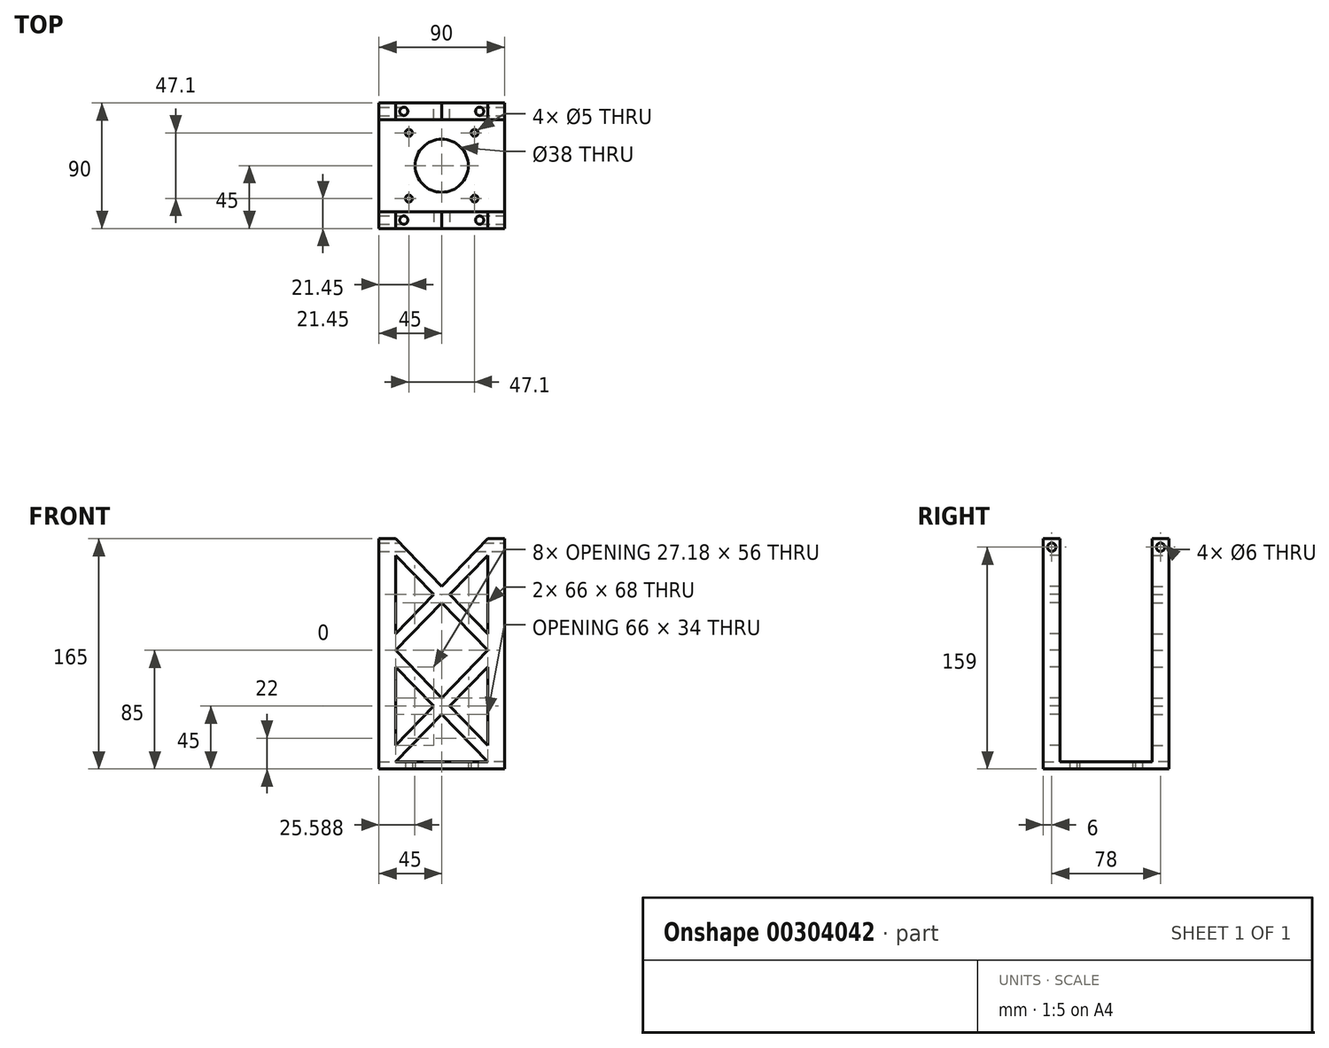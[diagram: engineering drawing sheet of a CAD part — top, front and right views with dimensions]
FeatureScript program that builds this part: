
annotation { "Feature Type Name" : "Feature", "Feature Type Description" : "" }
export const myFeature = defineFeature(function(context is Context, id is Id, definition is map)
    precondition{}
    {
        {
            var Q0;
            Q0=qCreatedBy(makeId("Top.planeOp"),FACE);
            var sketch = newSketch(context, id + "F0", { "sketchPlane" : qUnion([Q0])});
            skLineSegment(sketch, "E0.bottom", {"start": v(45, -45) * mm, "end": v(-45, -45) * mm});
            skLineSegment(sketch, "E0.top", {"start": v(45, 45) * mm, "end": v(-45, 45) * mm});
            skLineSegment(sketch, "E0.left", {"start": v(45, -45) * mm, "end": v(45, 45) * mm});
            skLineSegment(sketch, "E0.right", {"start": v(-45, -45) * mm, "end": v(-45, 45) * mm});
            skPoint(sketch, "E0.middle", {"position": v(0, 0) * mm});
            skLineSegment(sketch, "E1.bottom", {"start": v(23.55, -23.55) * mm, "end": v(-23.55, -23.55) * mm, "construction": true});
            skLineSegment(sketch, "E1.top", {"start": v(23.55, 23.55) * mm, "end": v(-23.55, 23.55) * mm, "construction": true});
            skLineSegment(sketch, "E1.left", {"start": v(23.55, -23.55) * mm, "end": v(23.55, 23.55) * mm, "construction": true});
            skLineSegment(sketch, "E1.right", {"start": v(-23.55, -23.55) * mm, "end": v(-23.55, 23.55) * mm, "construction": true});
            skCircle(sketch, "E2", {"center": v(0, 0) * mm, "radius": 19 * mm});
            skCircle(sketch, "E3", {"center": v(-23.55, 23.55) * mm, "radius": 2.5 * mm});
            skCircle(sketch, "E4", {"center": v(23.55, 23.55) * mm, "radius": 2.5 * mm});
            skCircle(sketch, "E5", {"center": v(23.55, -23.55) * mm, "radius": 2.5 * mm});
            skCircle(sketch, "E6", {"center": v(-23.55, -23.55) * mm, "radius": 2.5 * mm});
            skSolve(sketch);
        }
        {
            var Q0;
            Q0=makeQuery(id+"F0.imprint","IMPRINT",FACE,{"disambiguationData":[TD([[makeQuery(id+"F0.imprint","IMPRINT",EDGE,{"derivedFrom":sQuery(id+"F0.wireOp",EDGE,"E0.bottom")}),-1.0]])]});
            extrude(context, id + "F1", {"entities" : qUnion([Q0]), "depth" : 5 * mm});
        }
        {
            var Q0;
            Q0=makeQuery(id+"F1.opExtrude","CAP_FACE",FACE,{"disambiguationData":[OSD([sQuery(id+"F0.wireOp",EDGE,"E0.bottom"),sQuery(id+"F0.wireOp",EDGE,"E0.top"),sQuery(id+"F0.wireOp",EDGE,"E0.left"),sQuery(id+"F0.wireOp",EDGE,"E0.right"),sQuery(id+"F0.wireOp",EDGE,"E2"),sQuery(id+"F0.wireOp",EDGE,"E3"),sQuery(id+"F0.wireOp",EDGE,"E4"),sQuery(id+"F0.wireOp",EDGE,"E5"),sQuery(id+"F0.wireOp",EDGE,"E6")])],"isStart":false});
            cPlane(context, id + "F2", {"entities" : qUnion([Q0]), "cplaneType" : CPlaneType.OFFSET, "offset" : 0 * mm, "width" : 150 * mm, "height" : 150 * mm});
        }
        {
            var Q0;
            Q0=qCreatedBy(id+"F2.planeOp",FACE);
            var sketch = newSketch(context, id + "F3", { "sketchPlane" : qUnion([Q0])});
            skPoint(sketch, "E7.0", {"position": v(-45, -45) * mm});
            skLineSegment(sketch, "E8.bottom", {"start": v(-45, -45) * mm, "end": v(-33, -45) * mm});
            skLineSegment(sketch, "E8.top", {"start": v(-45, -33) * mm, "end": v(-33, -33) * mm});
            skLineSegment(sketch, "E8.left", {"start": v(-45, -45) * mm, "end": v(-45, -33) * mm});
            skLineSegment(sketch, "E8.right", {"start": v(-33, -45) * mm, "end": v(-33, -33) * mm});
            skPoint(sketch, "E9.1.0", {"position": v(45, -45) * mm});
            skLineSegment(sketch, "E9.1.1", {"start": v(45, -33) * mm, "end": v(33, -33) * mm});
            skLineSegment(sketch, "E9.1.2", {"start": v(45, -45) * mm, "end": v(33, -45) * mm});
            skLineSegment(sketch, "E9.1.3", {"start": v(33, -45) * mm, "end": v(33, -33) * mm});
            skLineSegment(sketch, "E9.1.4", {"start": v(45, -45) * mm, "end": v(45, -33) * mm});
            skPoint(sketch, "E9.2.0", {"position": v(45, 45) * mm});
            skLineSegment(sketch, "E9.2.1", {"start": v(33, 45) * mm, "end": v(33, 33) * mm});
            skLineSegment(sketch, "E9.2.2", {"start": v(45, 45) * mm, "end": v(45, 33) * mm});
            skLineSegment(sketch, "E9.2.3", {"start": v(45, 33) * mm, "end": v(33, 33) * mm});
            skLineSegment(sketch, "E9.2.4", {"start": v(45, 45) * mm, "end": v(33, 45) * mm});
            skPoint(sketch, "E9.3.0", {"position": v(-45, 45) * mm});
            skLineSegment(sketch, "E9.3.1", {"start": v(-45, 33) * mm, "end": v(-33, 33) * mm});
            skLineSegment(sketch, "E9.3.2", {"start": v(-45, 45) * mm, "end": v(-33, 45) * mm});
            skLineSegment(sketch, "E9.3.3", {"start": v(-33, 45) * mm, "end": v(-33, 33) * mm});
            skLineSegment(sketch, "E9.3.4", {"start": v(-45, 45) * mm, "end": v(-45, 33) * mm});
            skPoint(sketch, "E9.center", {"position": v(0, 0) * mm});
            skSolve(sketch);
        }
        {
            var Q0;
            Q0=makeQuery(id+"F3.imprint","IMPRINT",FACE,{"disambiguationData":[TD([[makeQuery(id+"F3.imprint","IMPRINT",EDGE,{"derivedFrom":sQuery(id+"F3.wireOp",EDGE,"E8.bottom")}),1.0]])]});
            var Q1;
            Q1=makeQuery(id+"F3.imprint","IMPRINT",FACE,{"disambiguationData":[TD([[makeQuery(id+"F3.imprint","IMPRINT",EDGE,{"derivedFrom":sQuery(id+"F3.wireOp",EDGE,"E9.1.1")}),1.0]])]});
            var Q2;
            Q2=makeQuery(id+"F3.imprint","IMPRINT",FACE,{"disambiguationData":[TD([[makeQuery(id+"F3.imprint","IMPRINT",EDGE,{"derivedFrom":sQuery(id+"F3.wireOp",EDGE,"E9.2.1")}),1.0]])]});
            var Q3;
            Q3=makeQuery(id+"F3.imprint","IMPRINT",FACE,{"disambiguationData":[TD([[makeQuery(id+"F3.imprint","IMPRINT",EDGE,{"derivedFrom":sQuery(id+"F3.wireOp",EDGE,"E9.3.1")}),1.0]])]});
            extrude(context, id + "F4", {"entities" : qUnion([Q0, Q1, Q2, Q3]), "operationType" : NewBodyOperationType.ADD, "depth" : 160 * mm});
        }
        {
            var Q0;
            Q0=makeQuery(id+"F4.boolean.opBoolean","MERGE",FACE,{"derivedFrom":[makeQuery(id+"F1.opExtrude","SWEPT_FACE",FACE,{"disambiguationData":[OSD([sQuery(id+"F0.wireOp",EDGE,"E0.bottom")])]}),makeQuery(id+"F4.opExtrude","SWEPT_FACE",FACE,{"disambiguationData":[OSD([sQuery(id+"F3.wireOp",EDGE,"E8.bottom")])]}),makeQuery(id+"F4.opExtrude","SWEPT_FACE",FACE,{"disambiguationData":[OSD([sQuery(id+"F3.wireOp",EDGE,"E9.1.2")])]})]});
            cPlane(context, id + "F5", {"entities" : qUnion([Q0]), "cplaneType" : CPlaneType.OFFSET, "offset" : 0 * mm, "width" : 150 * mm, "height" : 150 * mm});
        }
        {
            var Q0;
            Q0=qCreatedBy(id+"F5.planeOp",FACE);
            var sketch = newSketch(context, id + "F6", { "sketchPlane" : qUnion([Q0])});
            skPoint(sketch, "E10.0", {"position": v(-33, 5) * mm});
            skLineSegment(sketch, "E11", {"start": v(-33, 5) * mm, "end": v(-33, 17) * mm});
            skLineSegment(sketch, "E12", {"start": v(-33, 45) * mm, "end": v(33, 45) * mm, "construction": true});
            skLineSegment(sketch, "E13", {"start": v(0, 0) * mm, "end": v(0, 167.46) * mm, "construction": true});
            skLineSegment(sketch, "E14.0", {"start": v(-33, 85) * mm, "end": v(33, 85) * mm, "construction": true});
            skLineSegment(sketch, "E15.MirrorCS", {"start": v(33, 5) * mm, "end": v(33, 17) * mm});
            skLineSegment(sketch, "E16.MirrorCS", {"start": v(-33, 85) * mm, "end": v(-33, 73) * mm});
            skLineSegment(sketch, "E17.MirrorCS", {"start": v(33, 85) * mm, "end": v(33, 73) * mm});
            skLineSegment(sketch, "E18", {"start": v(-33, 5) * mm, "end": v(33, 73) * mm});
            skLineSegment(sketch, "E19", {"start": v(-33, 17) * mm, "end": v(33, 85) * mm});
            skLineSegment(sketch, "E20", {"start": v(33, 5) * mm, "end": v(-33, 73) * mm});
            skLineSegment(sketch, "E21", {"start": v(33, 17) * mm, "end": v(-33, 85) * mm});
            skLineSegment(sketch, "E22.MirrorCS", {"start": v(33, 153) * mm, "end": v(-33, 85) * mm});
            skLineSegment(sketch, "E23.MirrorCS", {"start": v(33, 165) * mm, "end": v(-33, 97) * mm});
            skLineSegment(sketch, "E24.MirrorCS", {"start": v(-33, 153) * mm, "end": v(33, 85) * mm});
            skLineSegment(sketch, "E25.MirrorCS", {"start": v(-33, 165) * mm, "end": v(33, 97) * mm});
            skLineSegment(sketch, "E26.MirrorCS", {"start": v(-33, 85) * mm, "end": v(-33, 97) * mm});
            skLineSegment(sketch, "E27.MirrorCS", {"start": v(-33, 165) * mm, "end": v(-33, 153) * mm});
            skLineSegment(sketch, "E28.MirrorCS", {"start": v(33, 165) * mm, "end": v(33, 153) * mm});
            skLineSegment(sketch, "E29.MirrorCS", {"start": v(33, 85) * mm, "end": v(33, 97) * mm});
            skSolve(sketch);
        }
        {
            var Q0;
            {var subQ0=sQuery(id+"F6.wireOp",EDGE,"E17.MirrorCS");Q0=makeQuery(id+"F6.imprint","IMPRINT",FACE,{"disambiguationData":[TD([[makeQuery(id+"F6.imprint","IMPRINT",EDGE,{"derivedFrom":subQ0}),-1.0]])]});}
            var Q1;
            {var subQ5=sQuery(id+"F6.wireOp",EDGE,"E29.MirrorCS");Q1=makeQuery(id+"F6.imprint","IMPRINT",FACE,{"disambiguationData":[TD([[makeQuery(id+"F6.imprint","IMPRINT",EDGE,{"derivedFrom":subQ5}),1.0]])]});}
            var Q2;
            {var subQ0=sQuery(id+"F6.wireOp",EDGE,"E28.MirrorCS");Q2=makeQuery(id+"F6.imprint","IMPRINT",FACE,{"disambiguationData":[TD([[makeQuery(id+"F6.imprint","IMPRINT",EDGE,{"derivedFrom":subQ0}),-1.0]])]});}
            var Q3;
            {var subQ5=sQuery(id+"F6.wireOp",EDGE,"E27.MirrorCS");Q3=makeQuery(id+"F6.imprint","IMPRINT",FACE,{"disambiguationData":[TD([[makeQuery(id+"F6.imprint","IMPRINT",EDGE,{"derivedFrom":subQ5}),1.0]])]});}
            var Q4;
            {var subQ0=sQuery(id+"F6.wireOp",EDGE,"E26.MirrorCS");Q4=makeQuery(id+"F6.imprint","IMPRINT",FACE,{"disambiguationData":[TD([[makeQuery(id+"F6.imprint","IMPRINT",EDGE,{"derivedFrom":subQ0}),-1.0]])]});}
            var Q5;
            {var subQ0=sQuery(id+"F6.wireOp",EDGE,"E25.MirrorCS");var subQ1=sQuery(id+"F6.wireOp",EDGE,"E22.MirrorCS");var subQ2=makeQuery(id+"F6.imprint","INTERSECT",VERTEX,{"derivedFrom":[subQ1,subQ0]});Q5=makeQuery(id+"F6.imprint","IMPRINT",FACE,{"disambiguationData":[TD([[makeQuery(id+"F6.imprint","IMPRINT",EDGE,{"disambiguationData":[TD([[subQ2,-1.0]])],"derivedFrom":subQ1}),-1.0]])]});}
            var Q6;
            {var subQ0=sQuery(id+"F6.wireOp",EDGE,"E20");var subQ1=sQuery(id+"F6.wireOp",EDGE,"E18");var subQ2=makeQuery(id+"F6.imprint","INTERSECT",VERTEX,{"derivedFrom":[subQ1,subQ0]});Q6=makeQuery(id+"F6.imprint","IMPRINT",FACE,{"disambiguationData":[TD([[makeQuery(id+"F6.imprint","IMPRINT",EDGE,{"disambiguationData":[TD([[subQ2,-1.0]])],"derivedFrom":subQ1}),1.0]])]});}
            var Q7;
            {var subQ0=sQuery(id+"F6.wireOp",EDGE,"E16.MirrorCS");Q7=makeQuery(id+"F6.imprint","IMPRINT",FACE,{"disambiguationData":[TD([[makeQuery(id+"F6.imprint","IMPRINT",EDGE,{"derivedFrom":subQ0}),1.0]])]});}
            var Q8;
            {var subQ0=sQuery(id+"F6.wireOp",EDGE,"E11");Q8=makeQuery(id+"F6.imprint","IMPRINT",FACE,{"disambiguationData":[TD([[makeQuery(id+"F6.imprint","IMPRINT",EDGE,{"derivedFrom":subQ0}),-1.0]])]});}
            var Q9;
            {var subQ0=sQuery(id+"F6.wireOp",EDGE,"E15.MirrorCS");Q9=makeQuery(id+"F6.imprint","IMPRINT",FACE,{"disambiguationData":[TD([[makeQuery(id+"F6.imprint","IMPRINT",EDGE,{"derivedFrom":subQ0}),1.0]])]});}
            extrude(context, id + "F7", {"entities" : qUnion([Q0, Q1, Q2, Q3, Q4, Q5, Q6, Q7, Q8, Q9]), "operationType" : NewBodyOperationType.ADD, "oppositeDirection" : true, "depth" : 12 * mm});
        }
        {
            var Q0;
            Q0=makeQuery(id+"F4.boolean.opBoolean","MERGE",FACE,{"derivedFrom":[makeQuery(id+"F1.opExtrude","SWEPT_FACE",FACE,{"disambiguationData":[OSD([sQuery(id+"F0.wireOp",EDGE,"E0.top")])]}),makeQuery(id+"F4.opExtrude","SWEPT_FACE",FACE,{"disambiguationData":[OSD([sQuery(id+"F3.wireOp",EDGE,"E9.2.4")])]}),makeQuery(id+"F4.opExtrude","SWEPT_FACE",FACE,{"disambiguationData":[OSD([sQuery(id+"F3.wireOp",EDGE,"E9.3.2")])]})]});
            cPlane(context, id + "F8", {"entities" : qUnion([Q0]), "cplaneType" : CPlaneType.OFFSET, "offset" : 0 * mm, "width" : 150 * mm, "height" : 150 * mm});
        }
        {
            var Q0;
            Q0=qCreatedBy(id+"F8.planeOp",FACE);
            var sketch = newSketch(context, id + "F9", { "sketchPlane" : qUnion([Q0])});
            skLineSegment(sketch, "E30.0", {"start": v(33, 85) * mm, "end": v(33, 97) * mm});
            skLineSegment(sketch, "E30.2", {"start": v(33, 153) * mm, "end": v(-33, 85) * mm});
            skLineSegment(sketch, "E30.3", {"start": v(33, 5) * mm, "end": v(33, 17) * mm});
            skLineSegment(sketch, "E30.4", {"start": v(33, 165) * mm, "end": v(-33, 97) * mm});
            skLineSegment(sketch, "E30.5", {"start": v(33, 165) * mm, "end": v(33, 153) * mm});
            skLineSegment(sketch, "E30.7", {"start": v(-33, 85) * mm, "end": v(-33, 73) * mm});
            skLineSegment(sketch, "E30.8", {"start": v(-33, 153) * mm, "end": v(33, 85) * mm});
            skLineSegment(sketch, "E30.9", {"start": v(-33, 5) * mm, "end": v(-33, 17) * mm});
            skLineSegment(sketch, "E30.10", {"start": v(33, 85) * mm, "end": v(33, 73) * mm});
            skLineSegment(sketch, "E30.11", {"start": v(-33, 17) * mm, "end": v(33, 85) * mm});
            skLineSegment(sketch, "E30.12", {"start": v(33, 5) * mm, "end": v(-33, 73) * mm});
            skLineSegment(sketch, "E30.13", {"start": v(-33, 85) * mm, "end": v(-33, 97) * mm});
            skLineSegment(sketch, "E30.14", {"start": v(33, 17) * mm, "end": v(-33, 85) * mm});
            skLineSegment(sketch, "E30.15", {"start": v(-33, 5) * mm, "end": v(33, 73) * mm});
            skLineSegment(sketch, "E30.16", {"start": v(-33, 165) * mm, "end": v(33, 97) * mm});
            skLineSegment(sketch, "E30.17", {"start": v(-33, 165) * mm, "end": v(-33, 153) * mm});
            skSolve(sketch);
        }
        {
            var Q0;
            {var subQ5=sQuery(id+"F9.wireOp",EDGE,"E30.17");Q0=makeQuery(id+"F9.imprint","IMPRINT",FACE,{"disambiguationData":[TD([[makeQuery(id+"F9.imprint","IMPRINT",EDGE,{"derivedFrom":subQ5}),1.0]])]});}
            var Q1;
            {var subQ0=sQuery(id+"F9.wireOp",EDGE,"E30.16");var subQ1=sQuery(id+"F9.wireOp",EDGE,"E30.2");var subQ2=makeQuery(id+"F9.imprint","INTERSECT",VERTEX,{"derivedFrom":[subQ1,subQ0]});Q1=makeQuery(id+"F9.imprint","IMPRINT",FACE,{"disambiguationData":[TD([[makeQuery(id+"F9.imprint","IMPRINT",EDGE,{"disambiguationData":[TD([[subQ2,-1.0]])],"derivedFrom":subQ1}),-1.0]])]});}
            var Q2;
            {var subQ0=sQuery(id+"F9.wireOp",EDGE,"E30.5");Q2=makeQuery(id+"F9.imprint","IMPRINT",FACE,{"disambiguationData":[TD([[makeQuery(id+"F9.imprint","IMPRINT",EDGE,{"derivedFrom":subQ0}),-1.0]])]});}
            var Q3;
            {var subQ0=sQuery(id+"F9.wireOp",EDGE,"E30.0");Q3=makeQuery(id+"F9.imprint","IMPRINT",FACE,{"disambiguationData":[TD([[makeQuery(id+"F9.imprint","IMPRINT",EDGE,{"derivedFrom":subQ0}),1.0]])]});}
            var Q4;
            {var subQ0=sQuery(id+"F9.wireOp",EDGE,"E30.13");Q4=makeQuery(id+"F9.imprint","IMPRINT",FACE,{"disambiguationData":[TD([[makeQuery(id+"F9.imprint","IMPRINT",EDGE,{"derivedFrom":subQ0}),-1.0]])]});}
            var Q5;
            {var subQ0=sQuery(id+"F9.wireOp",EDGE,"E30.7");Q5=makeQuery(id+"F9.imprint","IMPRINT",FACE,{"disambiguationData":[TD([[makeQuery(id+"F9.imprint","IMPRINT",EDGE,{"derivedFrom":subQ0}),1.0]])]});}
            var Q6;
            {var subQ0=sQuery(id+"F9.wireOp",EDGE,"E30.9");Q6=makeQuery(id+"F9.imprint","IMPRINT",FACE,{"disambiguationData":[TD([[makeQuery(id+"F9.imprint","IMPRINT",EDGE,{"derivedFrom":subQ0}),-1.0]])]});}
            var Q7;
            {var subQ0=sQuery(id+"F9.wireOp",EDGE,"E30.10");Q7=makeQuery(id+"F9.imprint","IMPRINT",FACE,{"disambiguationData":[TD([[makeQuery(id+"F9.imprint","IMPRINT",EDGE,{"derivedFrom":subQ0}),-1.0]])]});}
            var Q8;
            {var subQ0=sQuery(id+"F9.wireOp",EDGE,"E30.3");Q8=makeQuery(id+"F9.imprint","IMPRINT",FACE,{"disambiguationData":[TD([[makeQuery(id+"F9.imprint","IMPRINT",EDGE,{"derivedFrom":subQ0}),1.0]])]});}
            var Q9;
            {var subQ0=sQuery(id+"F9.wireOp",EDGE,"E30.12");var subQ1=sQuery(id+"F9.wireOp",EDGE,"E30.11");var subQ2=makeQuery(id+"F9.imprint","INTERSECT",VERTEX,{"derivedFrom":[subQ1,subQ0]});Q9=makeQuery(id+"F9.imprint","IMPRINT",FACE,{"disambiguationData":[TD([[makeQuery(id+"F9.imprint","IMPRINT",EDGE,{"disambiguationData":[TD([[subQ2,-1.0]])],"derivedFrom":subQ1}),-1.0]])]});}
            extrude(context, id + "F10", {"entities" : qUnion([Q0, Q1, Q2, Q3, Q4, Q5, Q6, Q7, Q8, Q9]), "operationType" : NewBodyOperationType.ADD, "oppositeDirection" : true, "depth" : 12 * mm});
        }
        {
            var Q0;
            Q0=makeQuery(id+"F4.boolean.opBoolean","MERGE",FACE,{"derivedFrom":[makeQuery(id+"F1.opExtrude","SWEPT_FACE",FACE,{"disambiguationData":[OSD([sQuery(id+"F0.wireOp",EDGE,"E0.left")])]}),makeQuery(id+"F4.opExtrude","SWEPT_FACE",FACE,{"disambiguationData":[OSD([sQuery(id+"F3.wireOp",EDGE,"E9.1.4")])]}),makeQuery(id+"F4.opExtrude","SWEPT_FACE",FACE,{"disambiguationData":[OSD([sQuery(id+"F3.wireOp",EDGE,"E9.2.2")])]})]});
            cPlane(context, id + "F11", {"entities" : qUnion([Q0]), "cplaneType" : CPlaneType.OFFSET, "offset" : 0 * mm, "width" : 150 * mm, "height" : 150 * mm});
        }
        {
            var Q0;
            Q0=qCreatedBy(id+"F11.planeOp",FACE);
            var sketch = newSketch(context, id + "F12", { "sketchPlane" : qUnion([Q0])});
            skCircle(sketch, "E31", {"center": v(-39, 159) * mm, "radius": 3 * mm});
            skCircle(sketch, "E32", {"center": v(39, 159) * mm, "radius": 3 * mm});
            skSolve(sketch);
        }
        {
            var Q0;
            Q0=makeQuery(id+"F12.imprint","IMPRINT",FACE,{"disambiguationData":[TD([[makeQuery(id+"F12.imprint","IMPRINT",EDGE,{"derivedFrom":sQuery(id+"F12.wireOp",EDGE,"E31")}),1.0]])]});
            var Q1;
            Q1=makeQuery(id+"F12.imprint","IMPRINT",FACE,{"disambiguationData":[TD([[makeQuery(id+"F12.imprint","IMPRINT",EDGE,{"derivedFrom":sQuery(id+"F12.wireOp",EDGE,"E32")}),1.0]])]});
            extrude(context, id + "F13", {"entities" : qUnion([Q0, Q1]), "operationType" : NewBodyOperationType.REMOVE, "endBound" : BoundingType.THROUGH_ALL, "oppositeDirection" : true, "depth" : 25 * mm});
        }
    });
